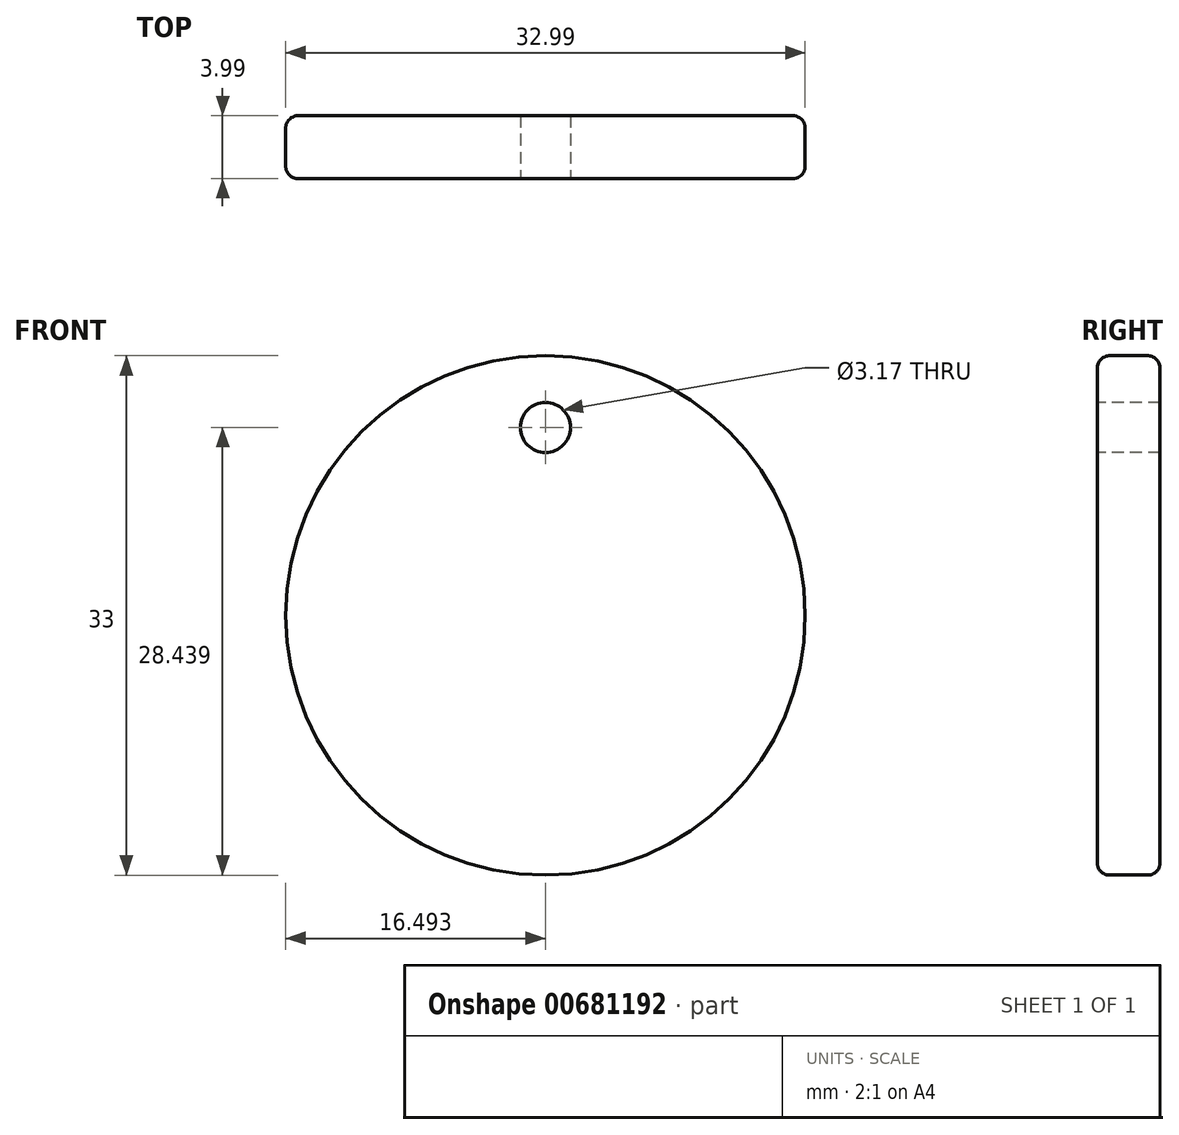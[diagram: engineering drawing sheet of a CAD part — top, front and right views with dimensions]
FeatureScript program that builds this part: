
annotation { "Feature Type Name" : "Feature", "Feature Type Description" : "" }
export const myFeature = defineFeature(function(context is Context, id is Id, definition is map)
    precondition{}
    {
        {
            var Q0;
            Q0=qCreatedBy(makeId("Front.planeOp"),FACE);
            var sketch = newSketch(context, id + "F0", { "sketchPlane" : qUnion([Q0])});
            skCircle(sketch, "E0", {"center": v(-24.26, 23.24) * mm, "radius": 16.5 * mm});
            skSolve(sketch);
        }
        {
            var Q0;
            Q0 = qSketchRegion(id + "F0", true);
            extrude(context, id + "F1", {"entities" : qUnion([Q0]), "depth" : 4 * mm, "offsetDistance" : 25.4 * mm});
        }
        {
            var Q0;
            Q0=makeQuery(id+"F1.opExtrude","CAP_EDGE",EDGE,{"disambiguationData":[OSD([sQuery(id+"F0.wireOp",EDGE,"E0")])],"isStart":true});
            var Q1;
            Q1=makeQuery(id+"F1.opExtrude","CAP_EDGE",EDGE,{"disambiguationData":[OSD([sQuery(id+"F0.wireOp",EDGE,"E0")])],"isStart":false});
            fillet(context, id + "F2", {"entities" : qUnion([Q0, Q1]), "radius" : 0.79 * mm, "tangentPropagation" : true, "allowEdgeOverflow" : false});
        }
        {
            var Q0;
            Q0=makeQuery(id+"F1.opExtrude","CAP_FACE",FACE,{"disambiguationData":[OSD([sQuery(id+"F0.wireOp",EDGE,"E0")])],"isStart":false});
            var sketch = newSketch(context, id + "F3", { "sketchPlane" : qUnion([Q0])});
            skCircle(sketch, "E1", {"center": v(-24.26, 35.18) * mm, "radius": 1.59 * mm});
            skSolve(sketch);
        }
        {
            var Q0;
            Q0 = qSketchRegion(id + "F3", true);
            extrude(context, id + "F4", {"entities" : qUnion([Q0]), "operationType" : NewBodyOperationType.REMOVE, "oppositeDirection" : true, "depth" : 25.4 * mm, "offsetDistance" : 25.4 * mm});
        }
    });
